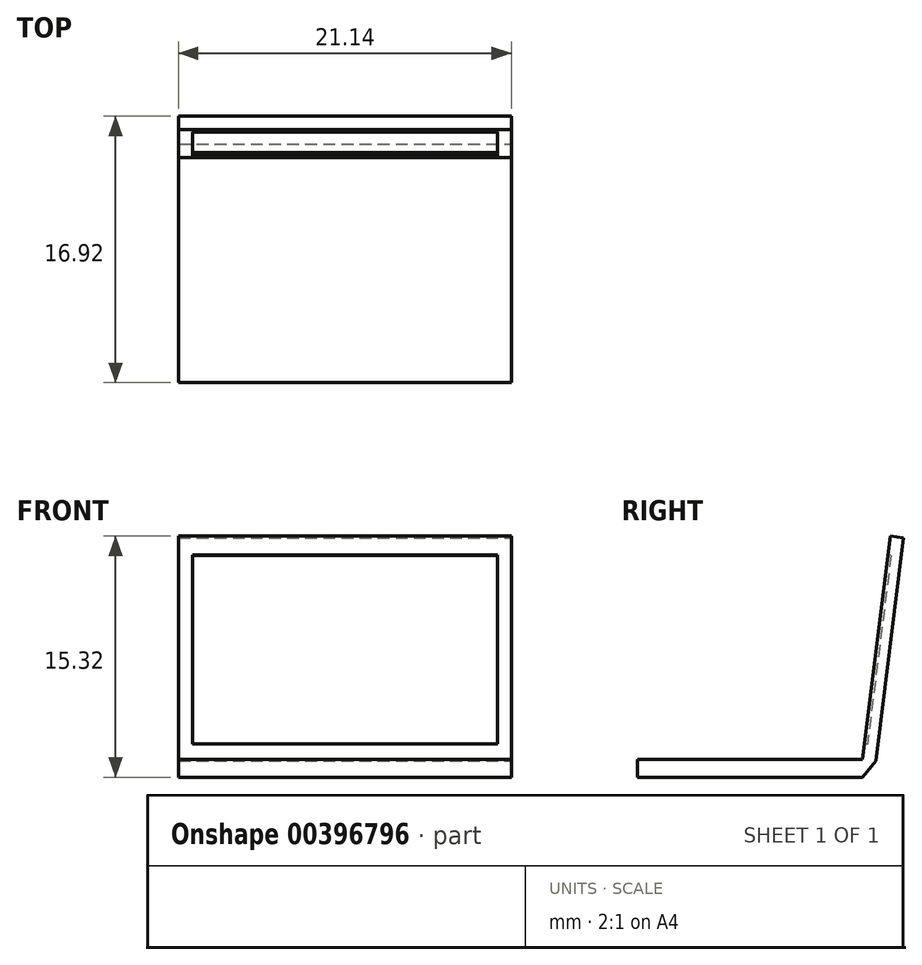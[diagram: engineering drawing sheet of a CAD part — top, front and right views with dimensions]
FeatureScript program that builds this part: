
annotation { "Feature Type Name" : "Feature", "Feature Type Description" : "" }
export const myFeature = defineFeature(function(context is Context, id is Id, definition is map)
    precondition{}
    {
        {
            assignVariable(context, id + "F0", {"name" : "SizeDivision", "anyValue" : 17.5});
        }
        {
            var Q0;
            Q0=qCreatedBy(makeId("Top.planeOp"),FACE);
            var sketch = newSketch(context, id + "F1", { "sketchPlane" : qUnion([Q0])});
            skLineSegment(sketch, "E0.bottom", {"start": v(0, 0) * mm, "end": v(21.14, 0) * mm});
            skLineSegment(sketch, "E0.top", {"start": v(0, -14.29) * mm, "end": v(21.14, -14.29) * mm});
            skLineSegment(sketch, "E0.left", {"start": v(0, 0) * mm, "end": v(0, -14.29) * mm});
            skLineSegment(sketch, "E0.right", {"start": v(21.14, 0) * mm, "end": v(21.14, -14.29) * mm});
            skSolve(sketch);
        }
        {
            var Q0;
            Q0 = qSketchRegion(id + "F1", true);
            extrude(context, id + "F2", {"entities" : qUnion([Q0]), "depth" : (20 / getVariable(context, 'SizeDivision')) * mm});
        }
        {
            var Q0;
            Q0=makeQuery(id+"F2.opExtrude","CAP_FACE",FACE,{"disambiguationData":[OSD([sQuery(id+"F1.wireOp",EDGE,"E0.bottom"),sQuery(id+"F1.wireOp",EDGE,"E0.top"),sQuery(id+"F1.wireOp",EDGE,"E0.left"),sQuery(id+"F1.wireOp",EDGE,"E0.right")])],"isStart":false});
            var sketch = newSketch(context, id + "F3", { "sketchPlane" : qUnion([Q0])});
            skLineSegment(sketch, "E1.bottom", {"start": v(0, 0) * mm, "end": v(21.14, 0) * mm});
            skLineSegment(sketch, "E1.top", {"start": v(0, -14.29) * mm, "end": v(21.14, -14.29) * mm});
            skLineSegment(sketch, "E1.left", {"start": v(0, 0) * mm, "end": v(0, -14.29) * mm});
            skLineSegment(sketch, "E1.right", {"start": v(21.14, 0) * mm, "end": v(21.14, -14.29) * mm});
            skSolve(sketch);
        }
        {
            var Q0;
            Q0 = qSketchRegion(id + "F3", true);
            extrude(context, id + "F4", {"entities" : qUnion([Q0]), "depth" : (15 / getVariable(context, 'SizeDivision')) * mm});
        }
        {
            var Q0;
            Q0=makeQuery(id+"F4.opExtrude","SWEPT_BODY",BODY,{"disambiguationData":[OSD([sQuery(id+"F3.wireOp",EDGE,"E1.bottom"),sQuery(id+"F3.wireOp",EDGE,"E1.top"),sQuery(id+"F3.wireOp",EDGE,"E1.left"),sQuery(id+"F3.wireOp",EDGE,"E1.right")])]});
            var Q1;
            Q1=makeQuery(id+"F2.opExtrude","CAP_EDGE",EDGE,{"disambiguationData":[OSD([sQuery(id+"F1.wireOp",EDGE,"E0.bottom")])],"isStart":false});
            transform(context, id + "F5", {"entities" : qUnion([Q0]), "transformType" : TransformType.ROTATION, "transformAxis" : qUnion([Q1]), "angle" : 97.14 * degree, "oppositeDirection" : true, "makeCopy" : false});
        }
        {
            var Q0;
            Q0=makeQuery(id+"F2.opExtrude","SWEPT_FACE",FACE,{"disambiguationData":[OSD([sQuery(id+"F1.wireOp",EDGE,"E0.left")])]});
            var sketch = newSketch(context, id + "F6", { "sketchPlane" : qUnion([Q0])});
            skLineSegment(sketch, "E2", {"start": v(0, 0) * mm, "end": v(-0.85, 1.04) * mm});
            skLineSegment(sketch, "E3", {"start": v(-0.85, 1.04) * mm, "end": v(0, 1.14) * mm});
            skLineSegment(sketch, "E4", {"start": v(0, 1.14) * mm, "end": v(0, 0) * mm});
            skSolve(sketch);
        }
        {
            var Q0;
            Q0 = qSketchRegion(id + "F6", true);
            var Q1;
            Q1=makeQuery(id+"F2.opExtrude","SWEPT_FACE",FACE,{"disambiguationData":[OSD([sQuery(id+"F1.wireOp",EDGE,"E0.right")])]});
            extrude(context, id + "F7", {"entities" : qUnion([Q0]), "operationType" : NewBodyOperationType.ADD, "endBound" : BoundingType.UP_TO_SURFACE, "oppositeDirection" : true, "endBoundEntityFace" : qUnion([Q1]), "depth" : 25 * mm});
        }
        {
            var Q0;
            Q0=makeQuery(id+"F4.opExtrude","CAP_FACE",FACE,{"disambiguationData":[OSD([sQuery(id+"F3.wireOp",EDGE,"E1.bottom"),sQuery(id+"F3.wireOp",EDGE,"E1.top"),sQuery(id+"F3.wireOp",EDGE,"E1.left"),sQuery(id+"F3.wireOp",EDGE,"E1.right")])],"isStart":true});
            var sketch = newSketch(context, id + "F8", { "sketchPlane" : qUnion([Q0])});
            skLineSegment(sketch, "E5.bottom", {"start": v(0.88, 14.22) * mm, "end": v(20.26, 14.22) * mm});
            skLineSegment(sketch, "E5.top", {"start": v(0.88, 2.12) * mm, "end": v(20.26, 2.12) * mm});
            skLineSegment(sketch, "E5.left", {"start": v(0.88, 14.22) * mm, "end": v(0.88, 2.12) * mm});
            skLineSegment(sketch, "E5.right", {"start": v(20.26, 14.22) * mm, "end": v(20.26, 2.12) * mm});
            skSolve(sketch);
        }
        {
            var Q0;
            Q0=makeQuery(id+"F8.imprint","IMPRINT",FACE,{"disambiguationData":[TD([[makeQuery(id+"F8.imprint","IMPRINT",EDGE,{"derivedFrom":sQuery(id+"F8.wireOp",EDGE,"E5.bottom")}),-1.0]])]});
            extrude(context, id + "F9", {"entities" : qUnion([Q0]), "operationType" : NewBodyOperationType.REMOVE, "oppositeDirection" : true, "depth" : 0.2 * mm});
        }
    });
